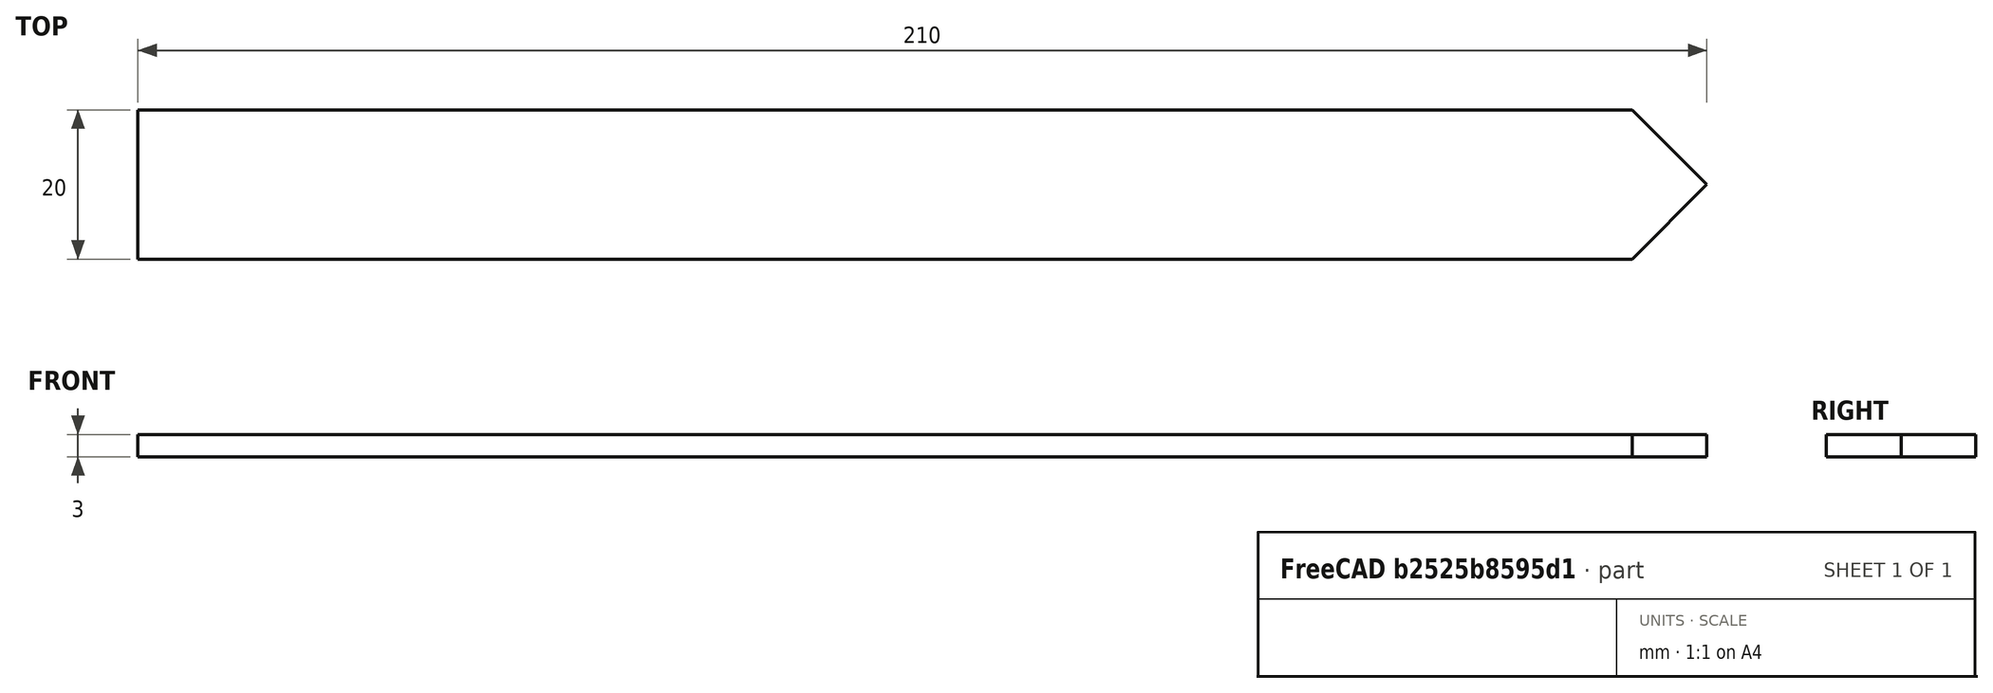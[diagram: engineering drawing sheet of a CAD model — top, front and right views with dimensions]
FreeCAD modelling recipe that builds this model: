
FCSTD DOCUMENT  (FreeCAD 0.20R29603 (Git))
Label: plant_label
License: All rights reserved
LicenseURL: http://en.wikipedia.org/wiki/All_rights_reserved
objects: Spreadsheet::Sheet×1, Sketcher::SketchObject×1, PartDesign::Pad×1, PartDesign::Body×1
note: 4 computed .brp shape members not serialized (recipe doc carries the construction recipe); baked Part::Feature solids carry a one-line shape summary decoded from their .brp

FEATURE [Spreadsheet::Sheet] Spreadsheet
  cells = A1=Length; B1(label_length)=200; A2=Width; B2(label_width)=20; A3=Thickness; B3(label_thickness)=3; A4=Spike length; B4(spike_length)=10
FEATURE [Sketcher::SketchObject] Sketch
  FullyConstrained = true
  MapMode = 5
  Support = -> [XY_Plane]
  expr: Constraints[20] = Spreadsheet.spike_length
  expr: Constraints[21] = Spreadsheet.label_length
  expr: Constraints[9] = Spreadsheet.label_width
  sketch-geometry (8):
    g0: LineSegment StartX=-105 StartY=10 StartZ=0 EndX=105 EndY=10 EndZ=0
    g1: LineSegment StartX=105 StartY=10 StartZ=0 EndX=105 EndY=-10 EndZ=0
    g2: LineSegment StartX=105 StartY=-10 StartZ=0 EndX=-105 EndY=-10 EndZ=0
    g3: LineSegment StartX=-105 StartY=-10 StartZ=0 EndX=-105 EndY=10 EndZ=0
    g4: LineSegment StartX=-105 StartY=10 StartZ=0 EndX=95 EndY=10 EndZ=0
    g5: LineSegment StartX=95 StartY=10 StartZ=0 EndX=105 EndY=0 EndZ=0
    g6: LineSegment StartX=105 StartY=0 StartZ=0 EndX=95 EndY=-10 EndZ=0
    g7: LineSegment StartX=95 StartY=-10 StartZ=0 EndX=-105 EndY=-10 EndZ=0
  constraints (22):
    c: Coincident(g0,g1)
    c: Coincident(g1,g2)
    c: Coincident(g2,g3)
    c: Coincident(g3,g0)
    c: Horizontal(g0)
    c: Horizontal(g2)
    c: Vertical(g1)
    c: Vertical(g3)
    c: Symmetric(g0,g1,g-1)
    c: Distance(g3) = 20
    c: Coincident(g3,g4)
    c: PointOnObject(g4,g0)
    c: Coincident(g4,g5)
    c: PointOnObject(g5,g-1)
    c: Coincident(g5,g6)
    c: PointOnObject(g6,g2)
    c: Coincident(g6,g7)
    c: Coincident(g7,g3)
    c: PointOnObject(g5,g1)
    c: Vertical(g4,g6)
    c: Distance(g4,g0) = 10
    c: Distance(g4) = 200
FEATURE [PartDesign::Pad] Pad  label="plant_label_body"
  Direction = (0,0,1)
  Length = 3
  Length2 = 10
  Profile = -> Sketch
  ReferenceAxis = -> Sketch [N_Axis]
  Type = 0
  expr: Length = Spreadsheet.label_thickness
FEATURE [PartDesign::Body] Body
  Group = -> [Sketch,Pad]
  Origin = -> Origin
  Tip = -> Pad
